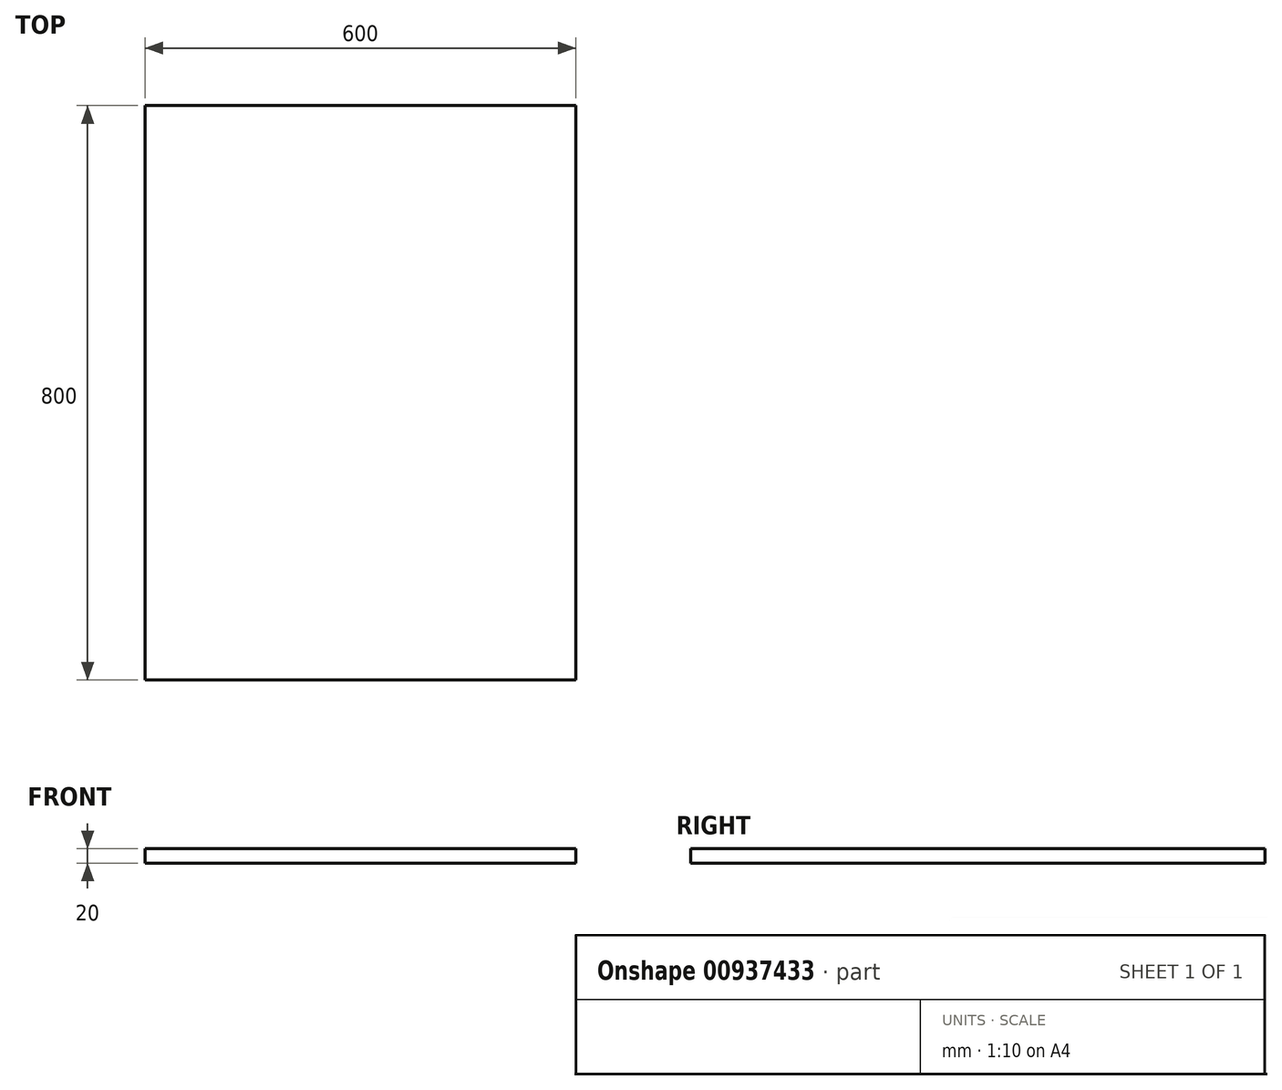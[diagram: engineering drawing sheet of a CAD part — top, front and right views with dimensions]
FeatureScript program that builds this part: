
annotation { "Feature Type Name" : "Feature", "Feature Type Description" : "" }
export const myFeature = defineFeature(function(context is Context, id is Id, definition is map)
    precondition{}
    {
        {
            var Q0;
            Q0=qCreatedBy(makeId("Top.planeOp"),FACE);
            var sketch = newSketch(context, id + "F0", { "sketchPlane" : qUnion([Q0])});
            skLineSegment(sketch, "E0.bottom", {"start": v(-300, 400) * mm, "end": v(300, 400) * mm});
            skLineSegment(sketch, "E0.top", {"start": v(-300, -400) * mm, "end": v(300, -400) * mm});
            skLineSegment(sketch, "E0.left", {"start": v(-300, 400) * mm, "end": v(-300, -400) * mm});
            skLineSegment(sketch, "E0.right", {"start": v(300, 400) * mm, "end": v(300, -400) * mm});
            skPoint(sketch, "E0.middle", {"position": v(0, 0) * mm});
            skSolve(sketch);
        }
        {
            var Q0;
            Q0 = qSketchRegion(id + "F0", true);
            extrude(context, id + "F1", {"entities" : qUnion([Q0]), "depth" : 20 * mm, "offsetDistance" : 25 * mm});
        }
    });
